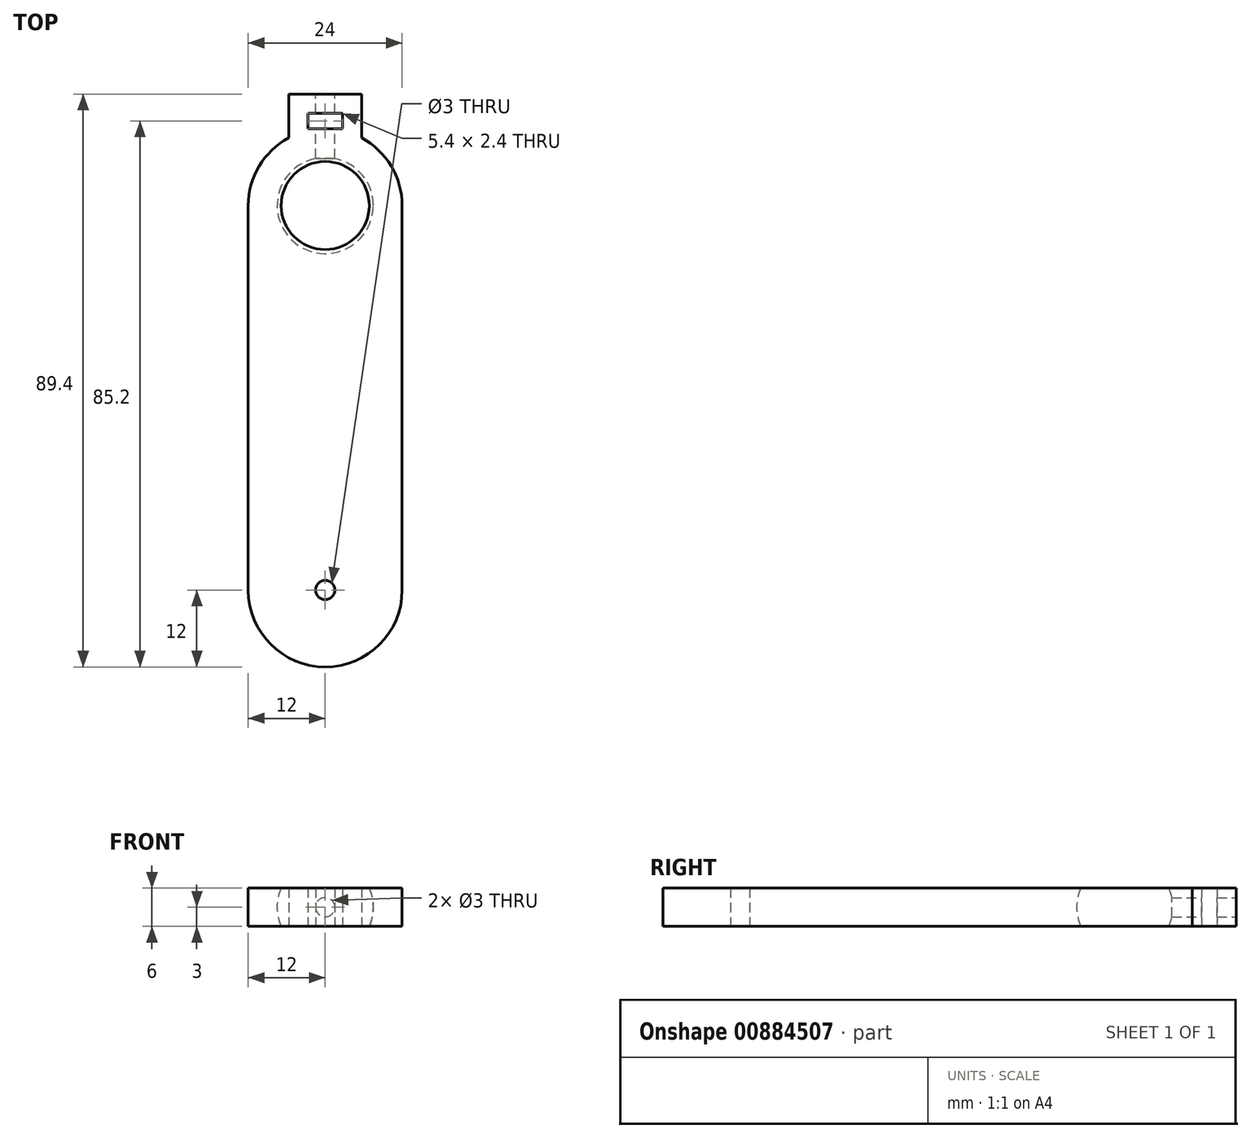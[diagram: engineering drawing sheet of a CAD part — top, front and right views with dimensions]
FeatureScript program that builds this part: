
annotation { "Feature Type Name" : "Feature", "Feature Type Description" : "" }
export const myFeature = defineFeature(function(context is Context, id is Id, definition is map)
    precondition{}
    {
        {
            var Q0;
            Q0=qCreatedBy(makeId("Top.planeOp"),FACE);
            var sketch = newSketch(context, id + "F0", { "sketchPlane" : qUnion([Q0])});
            skArc(sketch, "E0", {"start": v(-12, 0) * mm, "mid": v(0, -12) * mm, "end": v(12, 0) * mm});
            skArc(sketch, "E1", {"start": v(12, 60) * mm, "mid": v(0, 72) * mm, "end": v(-12, 60) * mm});
            skLineSegment(sketch, "E2", {"start": v(12, 0) * mm, "end": v(12, 60) * mm});
            skLineSegment(sketch, "E3", {"start": v(-12, 0) * mm, "end": v(-12, 60) * mm});
            skCircle(sketch, "E4", {"center": v(0, 0) * mm, "radius": 1.5 * mm});
            skSolve(sketch);
        }
        {
            var Q0;
            Q0 = qSketchRegion(id + "F0", true);
            extrude(context, id + "F1", {"entities" : qUnion([Q0]), "depth" : 6 * mm, "offsetDistance" : 25 * mm});
        }
        {
            var Q0;
            Q0=qCreatedBy(makeId("Right.planeOp"),FACE);
            var sketch = newSketch(context, id + "F2", { "sketchPlane" : qUnion([Q0])});
            skLineSegment(sketch, "E5", {"start": v(60, 10.5) * mm, "end": v(60, -4.5) * mm});
            skArc(sketch, "E6", {"start": v(60, -4.5) * mm, "mid": v(67.5, 3) * mm, "end": v(60, 10.5) * mm});
            skSolve(sketch);
        }
        {
            var Q0;
            Q0=makeQuery(id+"F1.opExtrude","CAP_FACE",FACE,{"disambiguationData":[OSD([sQuery(id+"F0.wireOp",EDGE,"E0"),sQuery(id+"F0.wireOp",EDGE,"E1"),sQuery(id+"F0.wireOp",EDGE,"E2"),sQuery(id+"F0.wireOp",EDGE,"E3"),sQuery(id+"F0.wireOp",EDGE,"E4")])],"isStart":true});
            var sketch = newSketch(context, id + "F3", { "sketchPlane" : qUnion([Q0])});
            skLineSegment(sketch, "E7.bottom", {"start": v(5.7, -77.4) * mm, "end": v(-5.7, -77.4) * mm});
            skLineSegment(sketch, "E7.top", {"start": v(5.7, -67.5) * mm, "end": v(-5.7, -67.5) * mm});
            skLineSegment(sketch, "E7.left", {"start": v(5.7, -77.4) * mm, "end": v(5.7, -67.5) * mm});
            skLineSegment(sketch, "E7.right", {"start": v(-5.7, -77.4) * mm, "end": v(-5.7, -67.5) * mm});
            skLineSegment(sketch, "E8.bottom", {"start": v(2.7, -74.4) * mm, "end": v(-2.7, -74.4) * mm});
            skLineSegment(sketch, "E8.top", {"start": v(2.7, -72) * mm, "end": v(-2.7, -72) * mm});
            skLineSegment(sketch, "E8.left", {"start": v(2.7, -74.4) * mm, "end": v(2.7, -72) * mm});
            skLineSegment(sketch, "E8.right", {"start": v(-2.7, -74.4) * mm, "end": v(-2.7, -72) * mm});
            skLineSegment(sketch, "E9", {"start": v(0, -74.4) * mm, "end": v(0, -77.4) * mm, "construction": true});
            skSolve(sketch);
        }
        {
            var Q0;
            Q0 = qSketchRegion(id + "F3", true);
            var Q1;
            Q1=makeQuery(id+"F1.opExtrude","CAP_FACE",FACE,{"disambiguationData":[OSD([sQuery(id+"F0.wireOp",EDGE,"E0"),sQuery(id+"F0.wireOp",EDGE,"E1"),sQuery(id+"F0.wireOp",EDGE,"E2"),sQuery(id+"F0.wireOp",EDGE,"E3"),sQuery(id+"F0.wireOp",EDGE,"E4")])],"isStart":false});
            extrude(context, id + "F4", {"entities" : qUnion([Q0]), "operationType" : NewBodyOperationType.ADD, "endBound" : BoundingType.UP_TO_SURFACE, "oppositeDirection" : true, "depth" : 25 * mm, "endBoundEntityFace" : qUnion([Q1]), "offsetDistance" : 25 * mm});
        }
        {
            var Q0;
            Q0=makeQuery(id+"F2.imprint","IMPRINT",FACE,{"disambiguationData":[TD([[makeQuery(id+"F2.imprint","IMPRINT",EDGE,{"derivedFrom":sQuery(id+"F2.wireOp",EDGE,"E5")}),1.0]])]});
            var Q1;
            Q1=sQuery(id+"F2.wireOp",EDGE,"E5");
            revolve(context, id + "F5", {"operationType" : NewBodyOperationType.REMOVE, "surfaceOperationType" : NewSurfaceOperationType.NEW, "entities" : qUnion([Q0]), "axis" : qUnion([Q1]), "revolveType" : RevolveType.FULL, "oppositeDirection" : true});
        }
        {
            var Q0;
            Q0=makeQuery(id+"F4.opExtrude","SWEPT_FACE",FACE,{"disambiguationData":[OSD([sQuery(id+"F3.wireOp",EDGE,"E7.bottom")])]});
            var sketch = newSketch(context, id + "F6", { "sketchPlane" : qUnion([Q0])});
            skLineSegment(sketch, "E10", {"start": v(-5.7, 6) * mm, "end": v(5.7, 0) * mm, "construction": true});
            skCircle(sketch, "E11", {"center": v(0, 3) * mm, "radius": 1.5 * mm});
            skSolve(sketch);
        }
        {
            var Q0;
            Q0 = qSketchRegion(id + "F6", true);
            var Q1;
            Q1=makeQuery(id+"F5.boolean.opBoolean","COPY",FACE,{"derivedFrom":makeQuery(id+"F5.opRevolve","SWEPT_FACE",FACE,{"disambiguationData":[OSD([sQuery(id+"F2.wireOp",EDGE,"E6")])]})});
            extrude(context, id + "F7", {"entities" : qUnion([Q0]), "operationType" : NewBodyOperationType.REMOVE, "endBound" : BoundingType.UP_TO_SURFACE, "oppositeDirection" : true, "depth" : 25 * mm, "endBoundEntityFace" : qUnion([Q1]), "offsetDistance" : 25 * mm});
        }
    });
